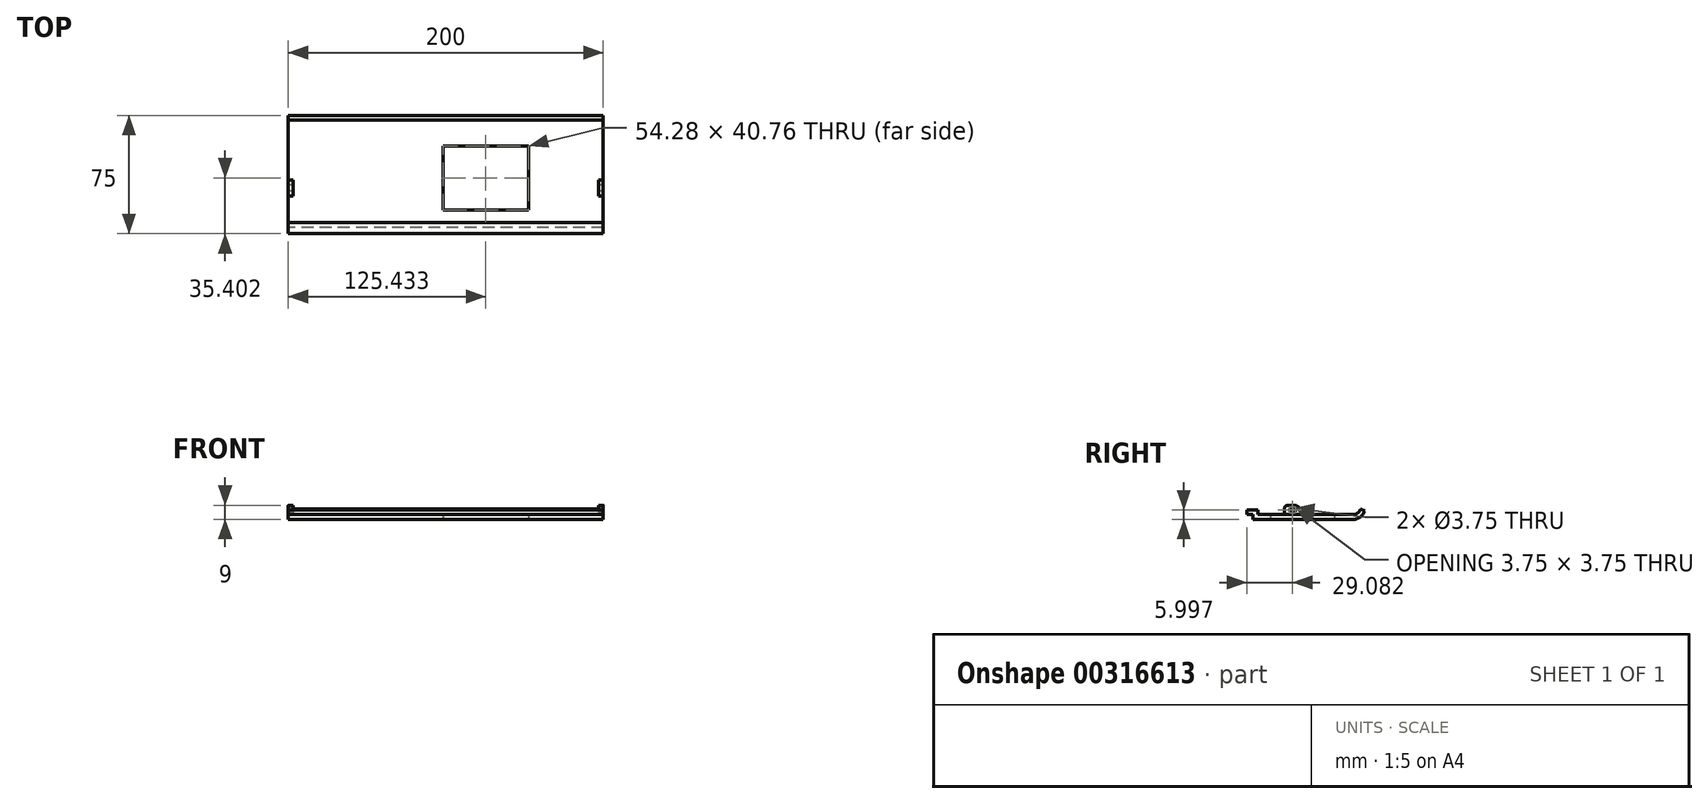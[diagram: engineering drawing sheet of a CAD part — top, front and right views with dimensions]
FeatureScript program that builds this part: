
annotation { "Feature Type Name" : "Feature", "Feature Type Description" : "" }
export const myFeature = defineFeature(function(context is Context, id is Id, definition is map)
    precondition{}
    {
        {
            var Q0;
            Q0=qCreatedBy(makeId("Right.planeOp"),FACE);
            var sketch = newSketch(context, id + "F0", { "sketchPlane" : qUnion([Q0])});
            skLineSegment(sketch, "E0.bottom", {"start": v(3.08, 3) * mm, "end": v(63.3, 3) * mm});
            skLineSegment(sketch, "E0.top", {"start": v(0, 0) * mm, "end": v(63.3, 0) * mm});
            skLineSegment(sketch, "E0.left", {"start": v(0, 3) * mm, "end": v(0, 0) * mm});
            skLineSegment(sketch, "E1.bottom", {"start": v(0, 3) * mm, "end": v(-4, 3) * mm});
            skLineSegment(sketch, "E1.top", {"start": v(3.08, 6) * mm, "end": v(-4, 6) * mm});
            skLineSegment(sketch, "E1.left", {"start": v(3.08, 3) * mm, "end": v(3.08, 6) * mm});
            skLineSegment(sketch, "E1.right", {"start": v(-4, 3) * mm, "end": v(-4, 6) * mm});
            skArc(sketch, "E2", {"start": v(63.3, 0) * mm, "mid": v(68.03, 1.51) * mm, "end": v(71, 5.5) * mm});
            skPoint(sketch, "E3", {"position": v(71.44, 8.1) * mm});
            skArc(sketch, "E4.0", {"start": v(63.3, 3) * mm, "mid": v(66.29, 3.96) * mm, "end": v(68.16, 6.47) * mm});
            skLineSegment(sketch, "E5", {"start": v(68.16, 6.47) * mm, "end": v(71, 5.5) * mm});
            skLineSegment(sketch, "E6", {"start": v(71, 5.5) * mm, "end": v(71, 0) * mm, "construction": true});
            skSolve(sketch);
        }
        {
            var Q0;
            Q0=makeQuery(id+"F0.imprint","IMPRINT",FACE,{"disambiguationData":[TD([[makeQuery(id+"F0.imprint","IMPRINT",EDGE,{"derivedFrom":sQuery(id+"F0.wireOp",EDGE,"E0.bottom")}),-1.0]])]});
            extrude(context, id + "F1", {"entities" : qUnion([Q0]), "depth" : 200 * mm});
        }
        {
            var Q0;
            Q0=makeQuery(id+"F1.opExtrude","CAP_FACE",FACE,{"disambiguationData":[OSD([sQuery(id+"F0.wireOp",EDGE,"E0.bottom"),sQuery(id+"F0.wireOp",EDGE,"E0.top"),sQuery(id+"F0.wireOp",EDGE,"E0.left"),sQuery(id+"F0.wireOp",EDGE,"E1.bottom"),sQuery(id+"F0.wireOp",EDGE,"E1.top"),sQuery(id+"F0.wireOp",EDGE,"E1.left"),sQuery(id+"F0.wireOp",EDGE,"E1.right"),sQuery(id+"F0.wireOp",EDGE,"E2"),sQuery(id+"F0.wireOp",EDGE,"E4.0"),sQuery(id+"F0.wireOp",EDGE,"E5")])],"isStart":false});
            var sketch = newSketch(context, id + "F2", { "sketchPlane" : qUnion([Q0])});
            skLineSegment(sketch, "E7.bottom", {"start": v(20, 3) * mm, "end": v(30, 3) * mm});
            skLineSegment(sketch, "E7.top", {"start": v(22, 9) * mm, "end": v(26, 9) * mm});
            skLineSegment(sketch, "E7.left", {"start": v(20, 3) * mm, "end": v(20, 7) * mm});
            skLineSegment(sketch, "E7.right", {"start": v(30, 3) * mm, "end": v(30, 5) * mm});
            skPoint(sketch, "E8.visualSharp", {"position": v(20, 9) * mm});
            skArc(sketch, "E8.filletArc", {"start": v(22, 9) * mm, "mid": v(20.59, 8.41) * mm, "end": v(20, 7) * mm});
            skPoint(sketch, "E9.visualSharp", {"position": v(30, 9) * mm});
            skArc(sketch, "E9.filletArc", {"start": v(30, 5) * mm, "mid": v(28.83, 7.83) * mm, "end": v(26, 9) * mm});
            skLineSegment(sketch, "E10", {"start": v(25.08, -1.75) * mm, "end": v(25.08, 15.47) * mm, "construction": true});
            skLineSegment(sketch, "E11", {"start": v(3.08, 6) * mm, "end": v(72.11, 6) * mm, "construction": true});
            skPoint(sketch, "E12", {"position": v(25.08, 6) * mm});
            skSolve(sketch);
        }
        {
            var Q0;
            Q0=qCreatedBy(makeId("Right.planeOp"),FACE);
            var sketch = newSketch(context, id + "F3", { "sketchPlane" : qUnion([Q0])});
            skCircle(sketch, "E13", {"center": v(25.08, 6) * mm, "radius": 1.88 * mm});
            skSolve(sketch);
        }
        {
            var Q0;
            Q0=makeQuery(id+"F2.imprint","IMPRINT",FACE,{"disambiguationData":[TD([[makeQuery(id+"F2.imprint","IMPRINT",EDGE,{"derivedFrom":sQuery(id+"F2.wireOp",EDGE,"E7.bottom")}),1.0]])]});
            extrude(context, id + "F4", {"entities" : qUnion([Q0]), "oppositeDirection" : true, "depth" : 200 * mm});
        }
        {
            var Q0;
            Q0=makeQuery(id+"F3.imprint","IMPRINT",FACE,{"disambiguationData":[TD([[makeQuery(id+"F3.imprint","IMPRINT",EDGE,{"derivedFrom":sQuery(id+"F3.wireOp",EDGE,"E13")}),1.0]])]});
            extrude(context, id + "F5", {"entities" : qUnion([Q0]), "operationType" : NewBodyOperationType.REMOVE, "endBound" : BoundingType.THROUGH_ALL, "depth" : 25 * mm});
        }
        {
            var Q0;
            Q0=makeQuery(id+"F4.opExtrude","SWEPT_FACE",FACE,{"disambiguationData":[OSD([sQuery(id+"F2.wireOp",EDGE,"E7.bottom")])]});
            var sketch = newSketch(context, id + "F6", { "sketchPlane" : qUnion([Q0])});
            skLineSegment(sketch, "E14.bottom", {"start": v(3, -20) * mm, "end": v(197, -20) * mm});
            skLineSegment(sketch, "E14.top", {"start": v(3, -30) * mm, "end": v(197, -30) * mm});
            skLineSegment(sketch, "E14.left", {"start": v(3, -20) * mm, "end": v(3, -30) * mm});
            skLineSegment(sketch, "E14.right", {"start": v(197, -20) * mm, "end": v(197, -30) * mm});
            skPoint(sketch, "E15", {"position": v(3, -30) * mm});
            skPoint(sketch, "E16", {"position": v(197, -30) * mm});
            skPoint(sketch, "E17", {"position": v(0, -30) * mm});
            skPoint(sketch, "E18", {"position": v(200, -30) * mm});
            skLineSegment(sketch, "E19.bottom", {"start": v(197, -20) * mm, "end": v(200, -20) * mm, "construction": true});
            skLineSegment(sketch, "E19.top", {"start": v(197, -30) * mm, "end": v(200, -30) * mm, "construction": true});
            skLineSegment(sketch, "E19.left", {"start": v(197, -20) * mm, "end": v(197, -30) * mm, "construction": true});
            skLineSegment(sketch, "E19.right", {"start": v(200, -20) * mm, "end": v(200, -30) * mm, "construction": true});
            skLineSegment(sketch, "E20.bottom", {"start": v(0, -20) * mm, "end": v(3, -20) * mm, "construction": true});
            skLineSegment(sketch, "E20.top", {"start": v(0, -30) * mm, "end": v(3, -30) * mm, "construction": true});
            skLineSegment(sketch, "E20.left", {"start": v(0, -20) * mm, "end": v(0, -30) * mm, "construction": true});
            skLineSegment(sketch, "E20.right", {"start": v(3, -20) * mm, "end": v(3, -30) * mm, "construction": true});
            skSolve(sketch);
        }
        {
            var Q0;
            Q0=makeQuery(id+"F6.imprint","IMPRINT",FACE,{"disambiguationData":[TD([[makeQuery(id+"F6.imprint","IMPRINT",EDGE,{"derivedFrom":sQuery(id+"F6.wireOp",EDGE,"E14.bottom")}),-1.0]])]});
            extrude(context, id + "F7", {"entities" : qUnion([Q0]), "operationType" : NewBodyOperationType.REMOVE, "oppositeDirection" : true, "depth" : 25 * mm});
        }
        {
            var Q0;
            Q0=makeQuery(id+"F1.opExtrude","SWEPT_FACE",FACE,{"disambiguationData":[OSD([sQuery(id+"F0.wireOp",EDGE,"E0.top")])]});
            var sketch = newSketch(context, id + "F8", { "sketchPlane" : qUnion([Q0])});
            skLineSegment(sketch, "E21.bottom", {"start": v(152.57, -51.78) * mm, "end": v(98.3, -51.78) * mm});
            skLineSegment(sketch, "E21.top", {"start": v(152.57, -11.02) * mm, "end": v(98.3, -11.02) * mm});
            skLineSegment(sketch, "E21.left", {"start": v(152.57, -51.78) * mm, "end": v(152.57, -11.02) * mm});
            skLineSegment(sketch, "E21.right", {"start": v(98.3, -51.78) * mm, "end": v(98.3, -11.02) * mm});
            skSolve(sketch);
        }
        {
            var Q0;
            Q0=makeQuery(id+"F8.imprint","IMPRINT",FACE,{"disambiguationData":[TD([[makeQuery(id+"F8.imprint","IMPRINT",EDGE,{"derivedFrom":sQuery(id+"F8.wireOp",EDGE,"E21.bottom")}),-1.0]])]});
            extrude(context, id + "F9", {"entities" : qUnion([Q0]), "operationType" : NewBodyOperationType.REMOVE, "endBound" : BoundingType.THROUGH_ALL, "oppositeDirection" : true, "depth" : 25 * mm});
        }
    });
